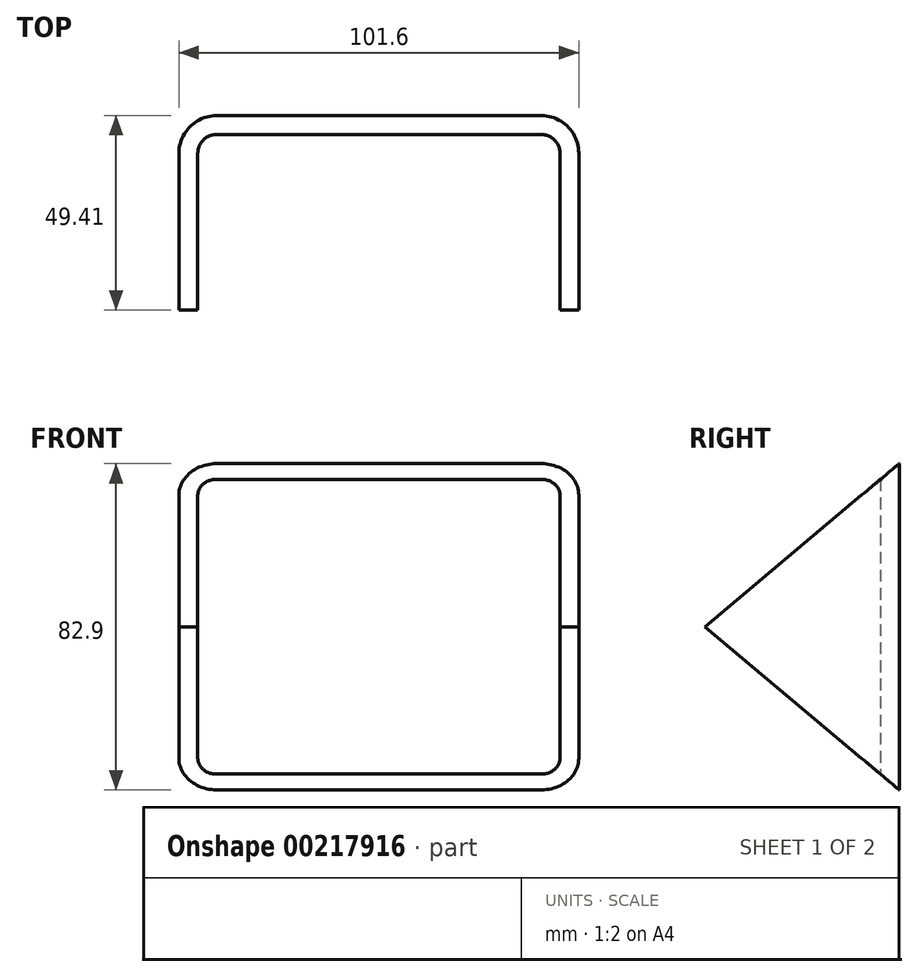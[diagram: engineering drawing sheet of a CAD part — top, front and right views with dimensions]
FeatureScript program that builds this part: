
annotation { "Feature Type Name" : "Feature", "Feature Type Description" : "" }
export const myFeature = defineFeature(function(context is Context, id is Id, definition is map)
    precondition{}
    {
        {
            var Q0;
            Q0=qCreatedBy(makeId("Top.planeOp"),FACE);
            var sketch = newSketch(context, id + "F0", { "sketchPlane" : qUnion([Q0])});
            skLineSegment(sketch, "E0.bottom", {"start": v(-25.23, 9.38) * mm, "end": v(-20.45, 9.38) * mm});
            skLineSegment(sketch, "E0.top", {"start": v(-15.68, 58.79) * mm, "end": v(66.82, 58.79) * mm});
            skLineSegment(sketch, "E0.left", {"start": v(-25.23, 9.38) * mm, "end": v(-25.23, 49.24) * mm});
            skLineSegment(sketch, "E0.right", {"start": v(76.37, 9.38) * mm, "end": v(76.37, 49.24) * mm});
            skPoint(sketch, "E1.visualSharp", {"position": v(-25.23, 58.79) * mm});
            skArc(sketch, "E1.filletArc", {"start": v(-15.68, 58.79) * mm, "mid": v(-22.43, 55.99) * mm, "end": v(-25.23, 49.24) * mm});
            skPoint(sketch, "E2.visualSharp", {"position": v(76.37, 58.79) * mm});
            skArc(sketch, "E2.filletArc", {"start": v(76.37, 49.24) * mm, "mid": v(73.58, 55.99) * mm, "end": v(66.82, 58.79) * mm});
            skLineSegment(sketch, "E3", {"start": v(-20.45, 9.38) * mm, "end": v(-20.45, 49.24) * mm});
            skLineSegment(sketch, "E4", {"start": v(-15.68, 54.01) * mm, "end": v(66.82, 54.01) * mm});
            skLineSegment(sketch, "E5", {"start": v(71.6, 49.24) * mm, "end": v(71.6, 9.38) * mm});
            skPoint(sketch, "E6.visualSharp", {"position": v(-20.45, 54.01) * mm});
            skArc(sketch, "E6.filletArc", {"start": v(-15.68, 54.01) * mm, "mid": v(-19.05, 52.61) * mm, "end": v(-20.45, 49.24) * mm});
            skPoint(sketch, "E7.visualSharp", {"position": v(71.6, 54.01) * mm});
            skArc(sketch, "E7.filletArc", {"start": v(71.6, 49.24) * mm, "mid": v(70.2, 52.61) * mm, "end": v(66.82, 54.01) * mm});
            skLineSegment(sketch, "E8.trimOffspring", {"start": v(71.6, 9.38) * mm, "end": v(76.37, 9.38) * mm});
            skSolve(sketch);
        }
        {
            var Q0;
            Q0 = qSketchRegion(id + "F0", true);
            extrude(context, id + "F1", {"entities" : qUnion([Q0]), "depth" : 88.9 * mm});
        }
        {
            var Q0;
            Q0=makeQuery(id+"F1.opExtrude","SWEPT_FACE",FACE,{"disambiguationData":[OSD([sQuery(id+"F0.wireOp",EDGE,"E0.left")])]});
            var sketch = newSketch(context, id + "F2", { "sketchPlane" : qUnion([Q0])});
            skLineSegment(sketch, "E9", {"start": v(-9.38, 44.45) * mm, "end": v(-78.12, -13.22) * mm});
            skLineSegment(sketch, "E10", {"start": v(-78.12, 102.12) * mm, "end": v(-9.38, 44.45) * mm});
            skLineSegment(sketch, "E11", {"start": v(-78.12, -13.22) * mm, "end": v(2, -13.22) * mm});
            skLineSegment(sketch, "E12", {"start": v(2, -13.22) * mm, "end": v(2, 102.12) * mm});
            skLineSegment(sketch, "E13", {"start": v(2, 102.12) * mm, "end": v(-78.12, 102.12) * mm});
            skSolve(sketch);
        }
        {
            var Q0;
            Q0 = qSketchRegion(id + "F2", true);
            extrude(context, id + "F3", {"entities" : qUnion([Q0]), "operationType" : NewBodyOperationType.REMOVE, "oppositeDirection" : true, "depth" : 127 * mm});
        }
    });
